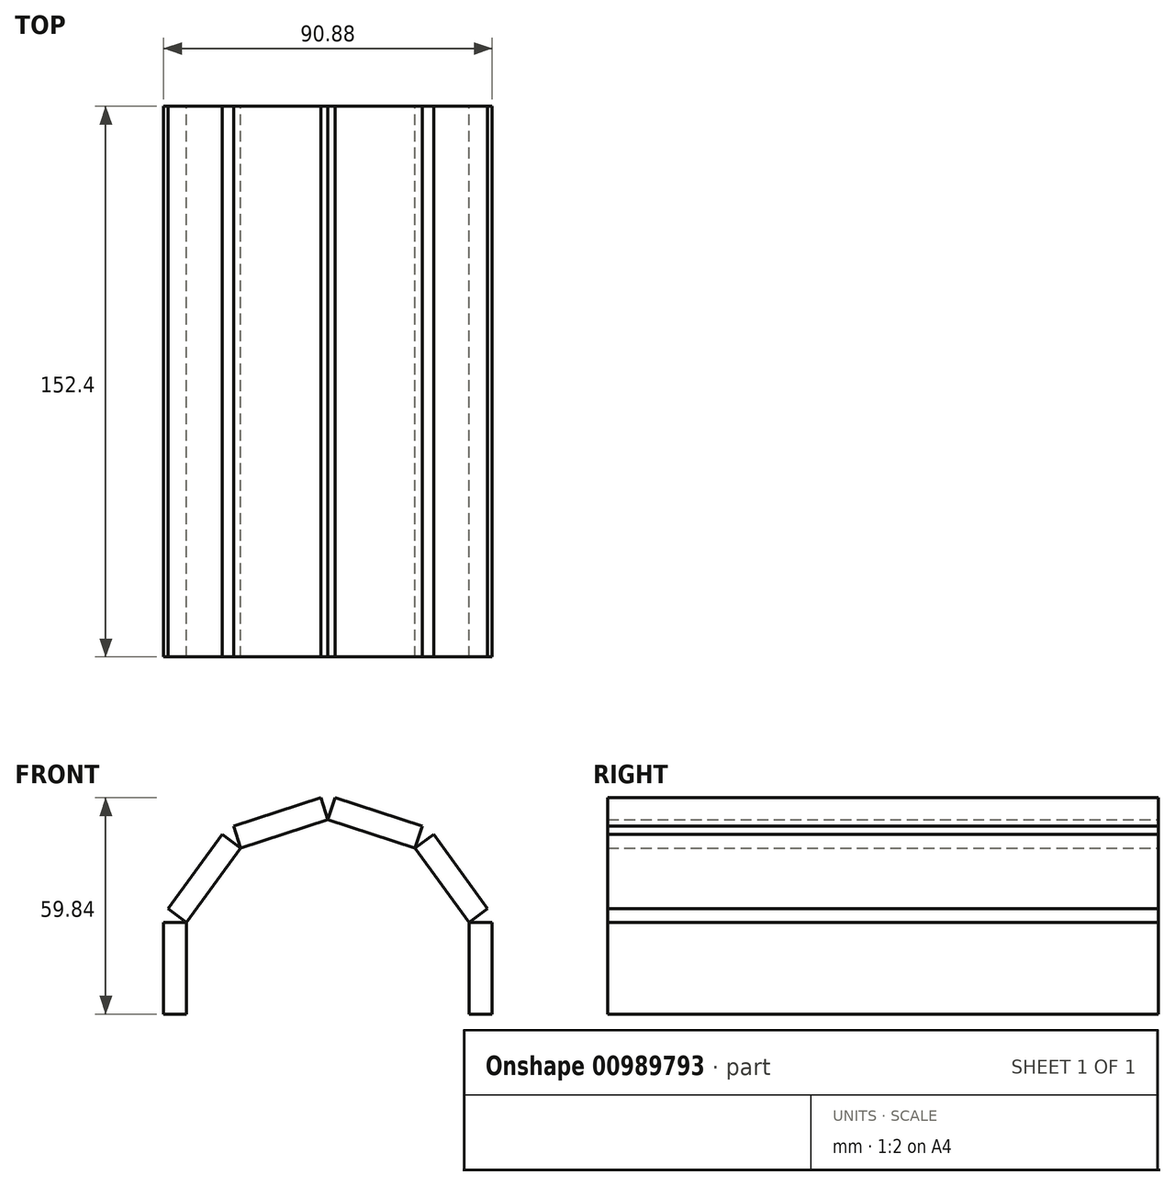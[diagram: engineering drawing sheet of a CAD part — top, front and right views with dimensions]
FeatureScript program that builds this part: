
annotation { "Feature Type Name" : "Feature", "Feature Type Description" : "" }
export const myFeature = defineFeature(function(context is Context, id is Id, definition is map)
    precondition{}
    {
        {
            var Q0;
            Q0=qCreatedBy(makeId("Front.planeOp"),FACE);
            var sketch = newSketch(context, id + "F0", { "sketchPlane" : qUnion([Q0])});
            skArc(sketch, "E0.cCircle", {"start": v(36.97, -12.7) * mm, "mid": v(0, 39.09) * mm, "end": v(-36.97, -12.7) * mm, "construction": true});
            skLineSegment(sketch, "E0.2", {"start": v(-39.09, -12.7) * mm, "end": v(-39.09, 12.7) * mm});
            skLineSegment(sketch, "E0.3", {"start": v(-39.09, 12.7) * mm, "end": v(-24.16, 33.25) * mm});
            skLineSegment(sketch, "E0.4", {"start": v(-24.16, 33.25) * mm, "end": v(0, 41.1) * mm});
            skLineSegment(sketch, "E0.5", {"start": v(0, 41.1) * mm, "end": v(24.16, 33.25) * mm});
            skLineSegment(sketch, "E0.6", {"start": v(24.16, 33.25) * mm, "end": v(39.09, 12.7) * mm});
            skLineSegment(sketch, "E0.7", {"start": v(39.09, 12.7) * mm, "end": v(39.09, -12.7) * mm});
            skLineSegment(sketch, "E1", {"start": v(39.09, -12.7) * mm, "end": v(-39.09, -12.7) * mm});
            skLineSegment(sketch, "E2.0", {"start": v(45.44, 14.76) * mm, "end": v(45.44, -12.7) * mm});
            skLineSegment(sketch, "E2.1", {"start": v(28.08, 38.65) * mm, "end": v(45.44, 14.76) * mm});
            skLineSegment(sketch, "E2.2", {"start": v(-45.44, -12.7) * mm, "end": v(-45.44, 14.76) * mm});
            skLineSegment(sketch, "E2.3", {"start": v(-45.44, 14.76) * mm, "end": v(-28.08, 38.65) * mm});
            skLineSegment(sketch, "E2.4", {"start": v(-28.08, 38.65) * mm, "end": v(0, 47.77) * mm});
            skLineSegment(sketch, "E2.5", {"start": v(0, 47.77) * mm, "end": v(28.08, 38.65) * mm});
            skLineSegment(sketch, "E3", {"start": v(-39.09, -12.7) * mm, "end": v(-45.44, -12.7) * mm});
            skLineSegment(sketch, "E4", {"start": v(-39.09, 12.7) * mm, "end": v(-45.44, 12.7) * mm});
            skLineSegment(sketch, "E5", {"start": v(-45.44, 12.7) * mm, "end": v(-39.09, 12.7) * mm});
            skLineSegment(sketch, "E6", {"start": v(-44.22, 16.43) * mm, "end": v(-39.09, 12.7) * mm});
            skLineSegment(sketch, "E7", {"start": v(-24.16, 33.25) * mm, "end": v(-29.3, 36.98) * mm});
            skLineSegment(sketch, "E8", {"start": v(-29.3, 36.98) * mm, "end": v(-24.16, 33.25) * mm});
            skLineSegment(sketch, "E9", {"start": v(-24.16, 33.25) * mm, "end": v(-26.12, 39.29) * mm});
            skLineSegment(sketch, "E10", {"start": v(0, 41.1) * mm, "end": v(-1.96, 47.14) * mm});
            skLineSegment(sketch, "E11", {"start": v(0, 41.1) * mm, "end": v(1.96, 47.14) * mm});
            skLineSegment(sketch, "E12", {"start": v(24.16, 33.25) * mm, "end": v(26.12, 39.29) * mm});
            skLineSegment(sketch, "E13", {"start": v(24.16, 33.25) * mm, "end": v(29.3, 36.98) * mm});
            skLineSegment(sketch, "E14", {"start": v(39.09, 12.7) * mm, "end": v(44.22, 16.43) * mm});
            skLineSegment(sketch, "E15", {"start": v(44.22, 16.43) * mm, "end": v(39.09, 12.7) * mm});
            skLineSegment(sketch, "E16", {"start": v(45.44, 12.7) * mm, "end": v(39.09, 12.7) * mm});
            skLineSegment(sketch, "E17", {"start": v(45.44, -12.7) * mm, "end": v(39.09, -12.7) * mm});
            skLineSegment(sketch, "E18", {"start": v(-44.22, 16.43) * mm, "end": v(-45.44, 12.7) * mm});
            skLineSegment(sketch, "E19", {"start": v(-29.3, 36.98) * mm, "end": v(-26.12, 39.29) * mm});
            skLineSegment(sketch, "E20", {"start": v(-1.96, 47.14) * mm, "end": v(1.96, 47.14) * mm});
            skLineSegment(sketch, "E21", {"start": v(26.12, 39.29) * mm, "end": v(29.3, 36.98) * mm});
            skLineSegment(sketch, "E22", {"start": v(44.22, 16.43) * mm, "end": v(45.44, 12.7) * mm});
            skLineSegment(sketch, "E23", {"start": v(0, 0) * mm, "end": v(39.09, 0) * mm, "construction": true});
            skSolve(sketch);
        }
        {
            var Q0;
            Q0=makeQuery(id+"F0.imprint","IMPRINT",FACE,{"disambiguationData":[TD([[makeQuery(id+"F0.imprint","IMPRINT",EDGE,{"derivedFrom":sQuery(id+"F0.wireOp",EDGE,"E0.2")}),1.0]])]});
            var Q1;
            Q1=makeQuery(id+"F0.imprint","IMPRINT",FACE,{"disambiguationData":[TD([[makeQuery(id+"F0.imprint","IMPRINT",EDGE,{"derivedFrom":sQuery(id+"F0.wireOp",EDGE,"E0.3")}),1.0]])]});
            var Q2;
            Q2=makeQuery(id+"F0.imprint","IMPRINT",FACE,{"disambiguationData":[TD([[makeQuery(id+"F0.imprint","IMPRINT",EDGE,{"derivedFrom":sQuery(id+"F0.wireOp",EDGE,"E0.4")}),1.0]])]});
            var Q3;
            Q3=makeQuery(id+"F0.imprint","IMPRINT",FACE,{"disambiguationData":[TD([[makeQuery(id+"F0.imprint","IMPRINT",EDGE,{"derivedFrom":sQuery(id+"F0.wireOp",EDGE,"E0.5")}),1.0]])]});
            var Q4;
            Q4=makeQuery(id+"F0.imprint","IMPRINT",FACE,{"disambiguationData":[TD([[makeQuery(id+"F0.imprint","IMPRINT",EDGE,{"derivedFrom":sQuery(id+"F0.wireOp",EDGE,"E0.6")}),1.0]])]});
            var Q5;
            Q5=makeQuery(id+"F0.imprint","IMPRINT",FACE,{"disambiguationData":[TD([[makeQuery(id+"F0.imprint","IMPRINT",EDGE,{"derivedFrom":sQuery(id+"F0.wireOp",EDGE,"E0.7")}),1.0]])]});
            extrude(context, id + "F1", {"entities" : qUnion([Q0, Q1, Q2, Q3, Q4, Q5]), "depth" : 152.4 * mm, "offsetDistance" : 25.4 * mm});
        }
    });
